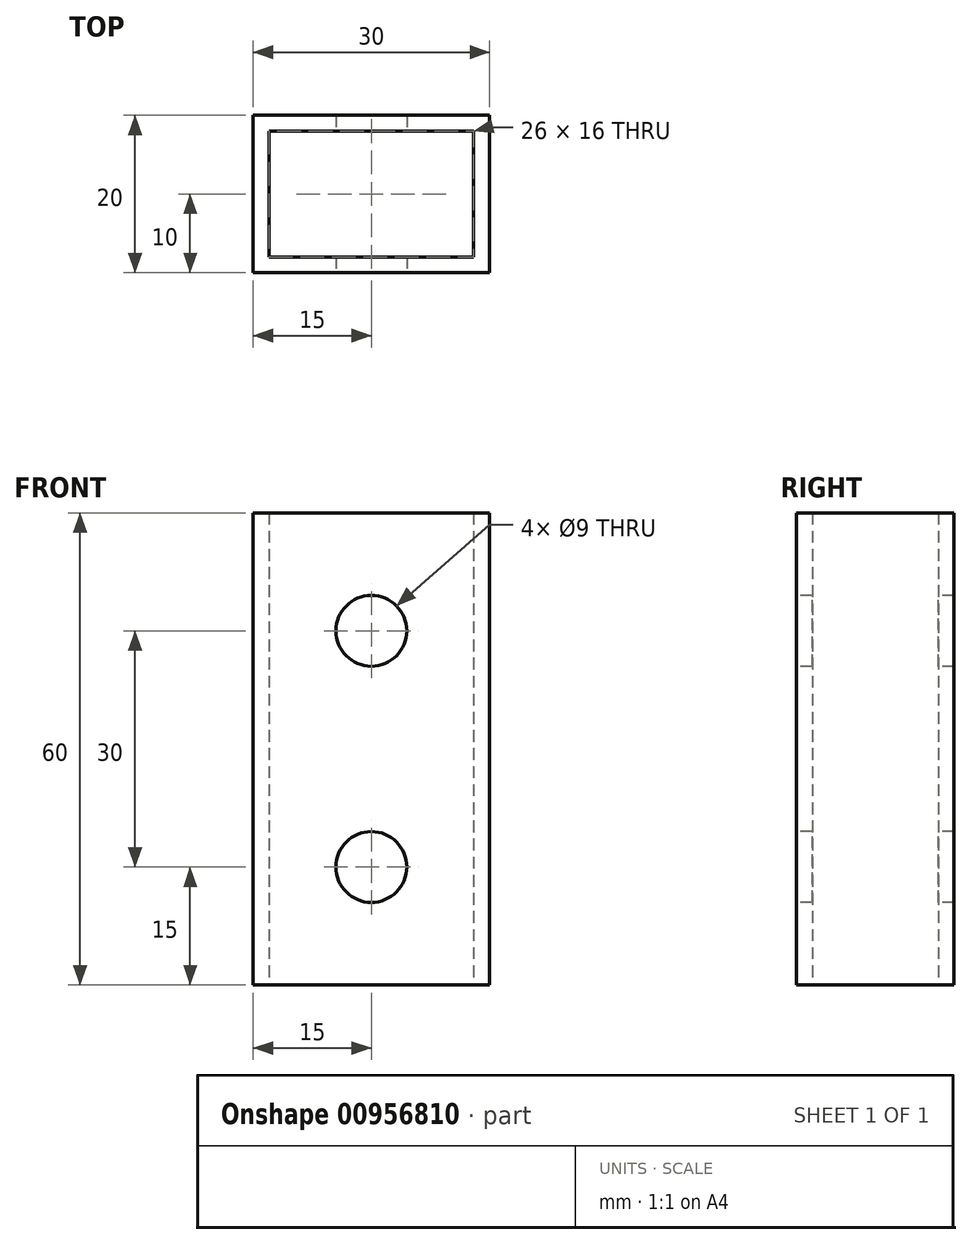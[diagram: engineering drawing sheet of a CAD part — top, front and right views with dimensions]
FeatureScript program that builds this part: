
annotation { "Feature Type Name" : "Feature", "Feature Type Description" : "" }
export const myFeature = defineFeature(function(context is Context, id is Id, definition is map)
    precondition{}
    {
        {
            var Q0;
            Q0=qCreatedBy(makeId("Top.planeOp"),FACE);
            var sketch = newSketch(context, id + "F0", { "sketchPlane" : qUnion([Q0])});
            skLineSegment(sketch, "E0.bottom", {"start": v(15, 10) * mm, "end": v(-15, 10) * mm});
            skLineSegment(sketch, "E0.top", {"start": v(15, -10) * mm, "end": v(-15, -10) * mm});
            skLineSegment(sketch, "E0.left", {"start": v(15, 10) * mm, "end": v(15, -10) * mm});
            skLineSegment(sketch, "E0.right", {"start": v(-15, 10) * mm, "end": v(-15, -10) * mm});
            skPoint(sketch, "E0.middle", {"position": v(0, 0) * mm});
            skLineSegment(sketch, "E1.bottom", {"start": v(13, 8) * mm, "end": v(-13, 8) * mm});
            skLineSegment(sketch, "E1.top", {"start": v(13, -8) * mm, "end": v(-13, -8) * mm});
            skLineSegment(sketch, "E1.left", {"start": v(13, 8) * mm, "end": v(13, -8) * mm});
            skLineSegment(sketch, "E1.right", {"start": v(-13, 8) * mm, "end": v(-13, -8) * mm});
            skSolve(sketch);
        }
        {
            var Q0;
            Q0 = qSketchRegion(id + "F0", true);
            extrude(context, id + "F1", {"entities" : qUnion([Q0]), "depth" : 60 * mm, "offsetDistance" : 25 * mm});
        }
        {
            var Q0;
            Q0=makeQuery(id+"F1.opExtrude","SWEPT_FACE",FACE,{"disambiguationData":[OSD([sQuery(id+"F0.wireOp",EDGE,"E0.top")])]});
            var sketch = newSketch(context, id + "F2", { "sketchPlane" : qUnion([Q0])});
            skCircle(sketch, "E2", {"center": v(0, 45) * mm, "radius": 4.5 * mm});
            skCircle(sketch, "E3", {"center": v(0, 15) * mm, "radius": 4.5 * mm});
            skLineSegment(sketch, "E4", {"start": v(0, 45) * mm, "end": v(0, 60) * mm, "construction": true});
            skLineSegment(sketch, "E5", {"start": v(0, 15) * mm, "end": v(0, 0) * mm, "construction": true});
            skSolve(sketch);
        }
        {
            var Q0;
            Q0 = qSketchRegion(id + "F2", true);
            var Q1;
            Q1=makeQuery(id+"F1.opExtrude","SWEPT_FACE",FACE,{"disambiguationData":[OSD([sQuery(id+"F0.wireOp",EDGE,"E0.bottom")])]});
            extrude(context, id + "F3", {"entities" : qUnion([Q0]), "operationType" : NewBodyOperationType.REMOVE, "endBound" : BoundingType.UP_TO_SURFACE, "oppositeDirection" : true, "depth" : 25 * mm, "endBoundEntityFace" : qUnion([Q1]), "offsetDistance" : 25 * mm});
        }
    });
